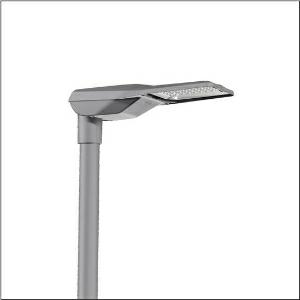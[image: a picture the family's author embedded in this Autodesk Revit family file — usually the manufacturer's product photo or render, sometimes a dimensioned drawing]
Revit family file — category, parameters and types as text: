
# Revit family: streetlight_sl_21_iq_mini___p0_8ab_5xe2r31g08gb_8bc5
name_source: partatom
category: Lighting Fixtures
units: mm (PartAtom-declared; Revit-internal decimal feet)

## family parameters
Cut with Voids When Loaded = No
Host = Face
Light Source = No
Part Type = Normal
Room Calculation Point = No
Round Connector Dimension = Use Diameter
Shared = No

## types (1)
- --- (1 x LED, 4930 lm, 37.1 W, 3000K)
    Apparent Load = 37 VA
    CIE Flux Codes = 36 71 98 100 100
    Color Rendering = 70
    Color Temperature = 3000K
    Default Elevation = 1800 mm
    Description = Streetlight SL 21 iQ mini, mast luminaire, primary light control with lens, of PMMA, primary optical cover: cover, of toughened safety glass, transparent, light distribution: P0.8aB, light emission: direct distribution, primary light characteristic: asymmetric, installation type: post-top, side-entry, LED, High Power LED, rated luminous flux: 4.930lm, luminous efficacy: 133lm/W, light colour: 730, colour temperature: 3000K, control gear: iQ Street-Remote, control: pre-setting: linear dimming characteristic, Street-Remote, Auto-Match, Temp-Guard, Lumen-Switch, Night-Set, Smart-Wire, Light-Fading, Desk-Remote (wireless, voltage-free reading and setting of iQ features in the workshop via application-optimized NFC function/RFID function), optimised constant luminous flux control (CLO 2.0), mains connection: 220..240V, AC, 50/60Hz, start of lifetime: 37W, end of service life: 39W, reduction: 18W, luminaire housing, of diecast aluminium, powder-coated, Siteco® metallic grey (DB 702S), corrosivity category C5 mid according to DIN EN ISO 12944, please order mast flange separately, inclination adjustable: 0°, 5°, 10°, 15°, sealing non-destructively replaceable, multi-level sealing system, length: 628mm, width: 235mm, height: 110mm, mast flange for spigot size: 42mm (side-entry): 5XC10008XM4, 60/48mm (side-entry/post-top): 5XC10108XM2, 76/60mm (side-entry/post-top): 5XC10108XM1, mounting height: 4..8m, protection rating (complete): IP66, insulation class (complete): insulation class II (safety insulation), certification: CE, ENEC, ENEC+, VDE, impact resistance: IK10, permissible operating ambient temperature for outdoor applications: -40..+50°C, standard-compliant lighting for roads and squares, packaging unit: 1 piece

Light Distribution: P0.8aB
    Height = 110 mm
    Lamp = 1 x LED
    Lamp Light Flux = 4930 lm
    Lamp Power = 37.1 W
    Lamp count = 1
    Length = 625 mm
    Luminous efficacy = 133 lm/W
    Manufacturer = Siteco
    ModVariant = No
    Model = 5XE2R31G08GB
    Number of Poles = 1
    OnlyDefault = Yes
    Power Factor = 1
    Product Name = Streetlight SL 21 iQ mini | P0.8aB
    Product group = mast luminaire | pylon top
    ProductGroupID = 6100
    Protection Class = Protection class II
    Protection Degree = IP 66
    RLX_Detail_Level = 1
    RLX_Emergency_Light_Flux = 0 lm
    RLX_Emergency_Type = 0
    RLX_Emergency_Type_DB = No
    RlxData = <blob elided: 26001 chars, md5=27194825>
    Socket = socket
    Standby Power = 0 W
    System Light Flux = 4930 lm
    System Power = 37 W
    Type Comments = factory setting: luminous flux: 100 % | dim-lin: 254 | 385 mA
    Type Image = l_1003519.jpg
    URL = http://relux.com
    VarID = @adj_074522
    Voltage = 0 V
    Weight = 0.00 kg
    Width = 234 mm

## geometry (parser evidence)
native form markers: Blend x4, Sweep x10
no freeform markers — native parametric forms only
